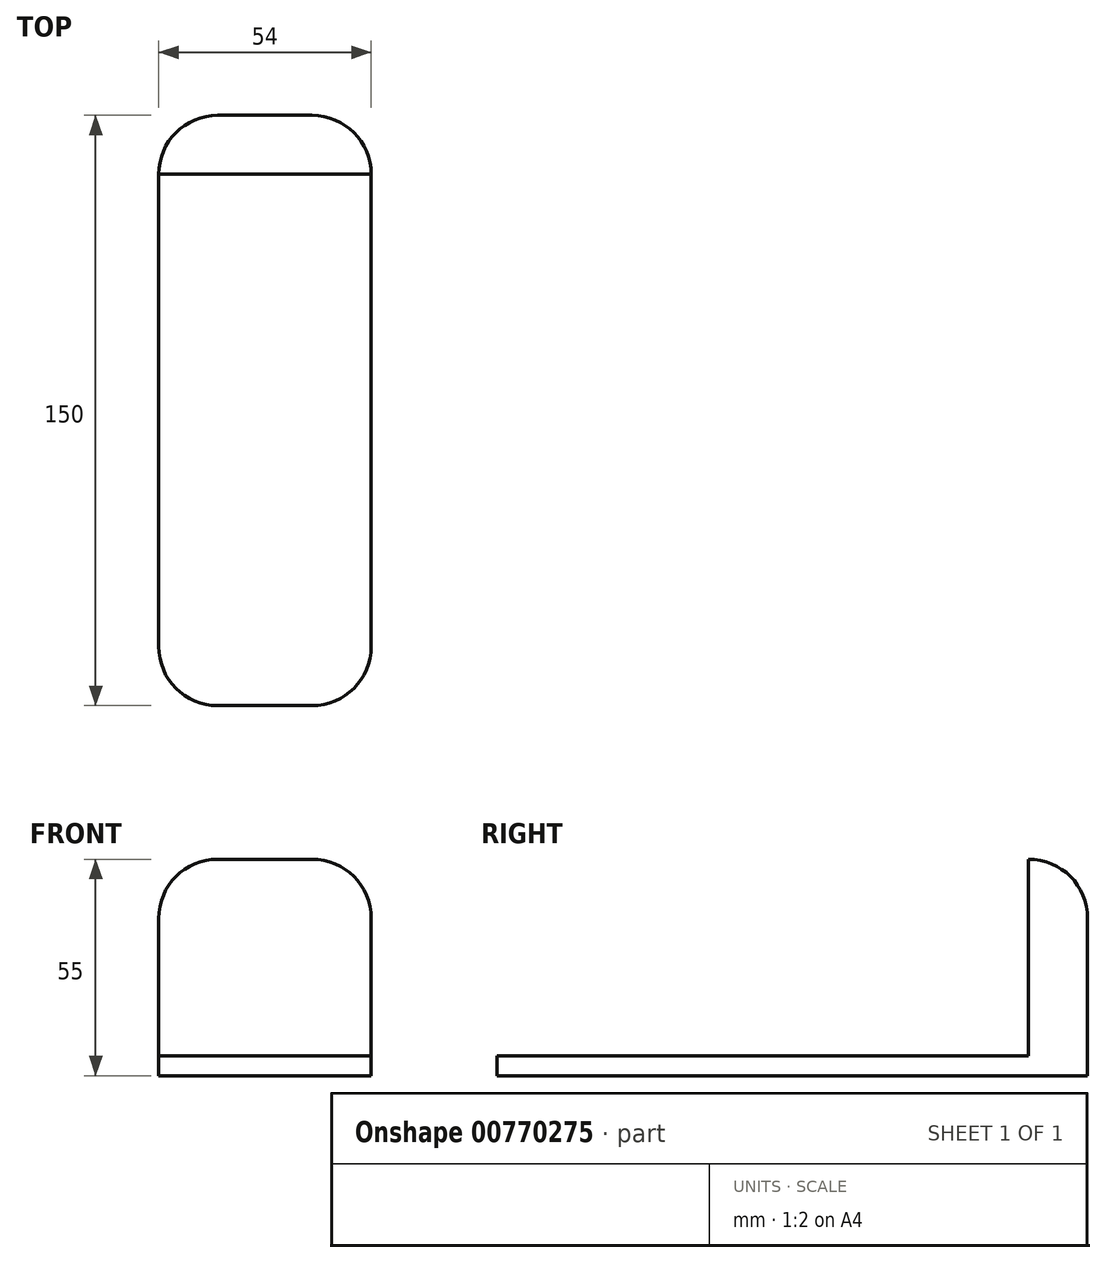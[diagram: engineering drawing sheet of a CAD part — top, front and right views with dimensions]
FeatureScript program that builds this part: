
annotation { "Feature Type Name" : "Feature", "Feature Type Description" : "" }
export const myFeature = defineFeature(function(context is Context, id is Id, definition is map)
    precondition{}
    {
        {
            var Q0;
            Q0=qCreatedBy(makeId("Top.planeOp"),FACE);
            var sketch = newSketch(context, id + "F0", { "sketchPlane" : qUnion([Q0])});
            skLineSegment(sketch, "E0.bottom", {"start": v(27, 75) * mm, "end": v(-27, 75) * mm});
            skLineSegment(sketch, "E0.top", {"start": v(27, -75) * mm, "end": v(-27, -75) * mm});
            skLineSegment(sketch, "E0.left", {"start": v(27, 75) * mm, "end": v(27, -75) * mm});
            skLineSegment(sketch, "E0.right", {"start": v(-27, 75) * mm, "end": v(-27, -75) * mm});
            skPoint(sketch, "E0.middle", {"position": v(0, 0) * mm});
            skSolve(sketch);
        }
        {
            var Q0;
            Q0 = qSketchRegion(id + "F0", true);
            extrude(context, id + "F1", {"entities" : qUnion([Q0]), "depth" : 50 * mm, "offsetDistance" : 25 * mm});
        }
        {
            var Q0;
            Q0=makeQuery(id+"F1.opExtrude","SWEPT_EDGE",EDGE,{"disambiguationData":[OSD([sQuery(id+"F0.wireOp",EDGE,"E0.top"),sQuery(id+"F0.wireOp",EDGE,"E0.left")])]});
            var Q1;
            Q1=makeQuery(id+"F1.opExtrude","SWEPT_EDGE",EDGE,{"disambiguationData":[OSD([sQuery(id+"F0.wireOp",EDGE,"E0.top"),sQuery(id+"F0.wireOp",EDGE,"E0.right")])]});
            var Q2;
            Q2=makeQuery(id+"F1.opExtrude","SWEPT_EDGE",EDGE,{"disambiguationData":[OSD([sQuery(id+"F0.wireOp",EDGE,"E0.bottom"),sQuery(id+"F0.wireOp",EDGE,"E0.left")])]});
            var Q3;
            Q3=makeQuery(id+"F1.opExtrude","SWEPT_EDGE",EDGE,{"disambiguationData":[OSD([sQuery(id+"F0.wireOp",EDGE,"E0.bottom"),sQuery(id+"F0.wireOp",EDGE,"E0.right")])]});
            fillet(context, id + "F2", {"entities" : qUnion([Q0, Q1, Q2, Q3]), "radius" : 15 * mm, "tangentPropagation" : true, "allowEdgeOverflow" : false});
        }
        {
            var Q0;
            Q0=makeQuery(id+"F1.opExtrude","CAP_EDGE",EDGE,{"disambiguationData":[OSD([sQuery(id+"F0.wireOp",EDGE,"E0.right")])],"isStart":false});
            fillet(context, id + "F3", {"entities" : qUnion([Q0]), "radius" : 15 * mm, "tangentPropagation" : true, "allowEdgeOverflow" : false});
        }
        {
            var Q0;
            Q0=makeQuery(id+"F1.opExtrude","CAP_FACE",FACE,{"disambiguationData":[OSD([sQuery(id+"F0.wireOp",EDGE,"E0.bottom"),sQuery(id+"F0.wireOp",EDGE,"E0.top"),sQuery(id+"F0.wireOp",EDGE,"E0.left"),sQuery(id+"F0.wireOp",EDGE,"E0.right")])],"isStart":true});
            var sketch = newSketch(context, id + "F4", { "sketchPlane" : qUnion([Q0])});
            skSolve(sketch);
        }
        {
            var Q0;
            {var subQ3=sQuery(id+"F0.wireOp",EDGE,"E0.bottom");Q0=makeQuery(id+"F4.imprint","IMPRINT",FACE,{"disambiguationData":[TD([[makeQuery(id+"F4.imprint","IMPRINT",EDGE,{"derivedFrom":makeQuery(id+"F1.opExtrude","CAP_EDGE",EDGE,{"disambiguationData":[OSD([subQ3])],"isStart":true})}),-1.0]])]});}
            extrude(context, id + "F5", {"entities" : qUnion([Q0]), "operationType" : NewBodyOperationType.ADD, "depth" : 5 * mm, "offsetDistance" : 25 * mm});
        }
        {
            var Q0;
            Q0=qCreatedBy(makeId("Top.planeOp"),FACE);
            var sketch = newSketch(context, id + "F6", { "sketchPlane" : qUnion([Q0])});
            skLineSegment(sketch, "E1.bottom", {"start": v(-62, -99.27) * mm, "end": v(59.1, -99.27) * mm});
            skLineSegment(sketch, "E1.top", {"start": v(-62, 60) * mm, "end": v(59.1, 60) * mm});
            skLineSegment(sketch, "E1.left", {"start": v(-62, -99.27) * mm, "end": v(-62, 60) * mm});
            skLineSegment(sketch, "E1.right", {"start": v(59.1, -99.27) * mm, "end": v(59.1, 60) * mm});
            skSolve(sketch);
        }
        {
            var Q0;
            Q0 = qSketchRegion(id + "F6", true);
            extrude(context, id + "F7", {"entities" : qUnion([Q0]), "operationType" : NewBodyOperationType.REMOVE, "endBound" : BoundingType.THROUGH_ALL, "depth" : 25 * mm, "offsetDistance" : 25 * mm});
        }
    });
